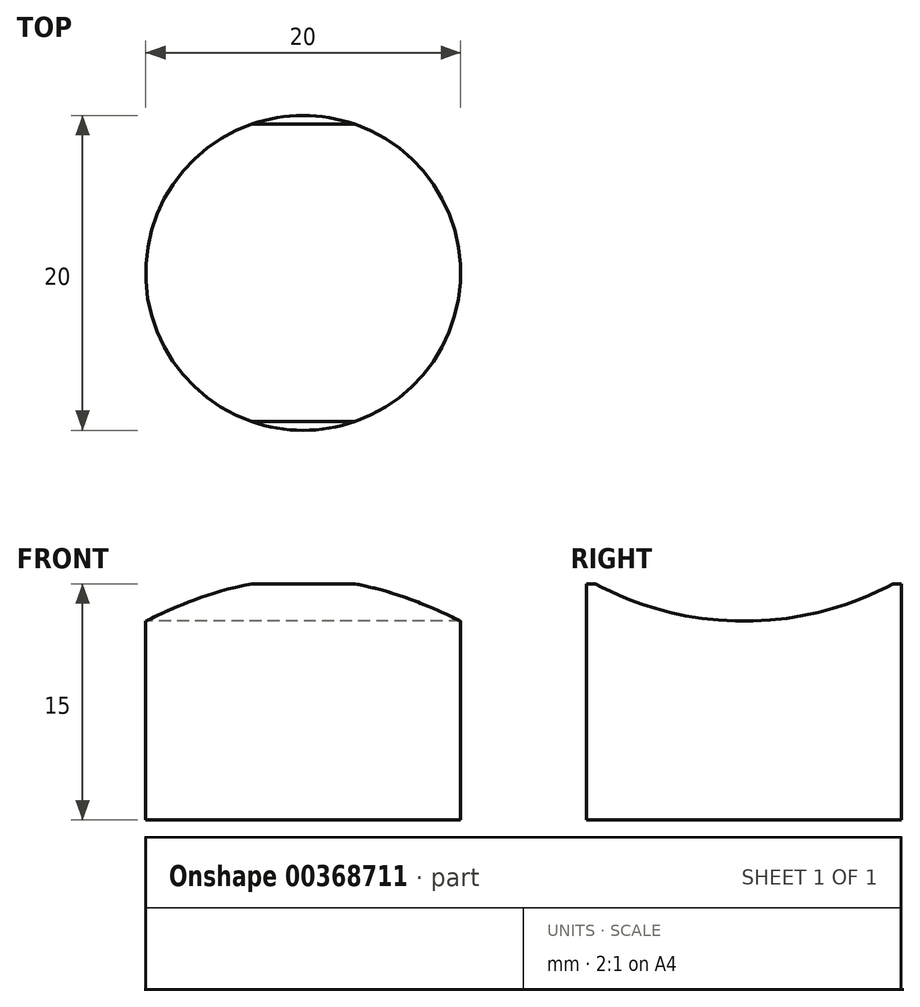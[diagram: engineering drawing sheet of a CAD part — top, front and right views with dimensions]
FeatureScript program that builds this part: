
annotation { "Feature Type Name" : "Feature", "Feature Type Description" : "" }
export const myFeature = defineFeature(function(context is Context, id is Id, definition is map)
    precondition{}
    {
        {
            var Q0;
            Q0=qCreatedBy(makeId("Top.planeOp"),FACE);
            var sketch = newSketch(context, id + "F0", { "sketchPlane" : qUnion([Q0])});
            skCircle(sketch, "E0", {"center": v(0, 0) * mm, "radius": 10 * mm});
            skSolve(sketch);
        }
        {
            var Q0;
            Q0 = qSketchRegion(id + "F0", true);
            extrude(context, id + "F1", {"entities" : qUnion([Q0]), "depth" : 15 * mm});
        }
        {
            var Q0;
            Q0=qCreatedBy(makeId("Right.planeOp"),FACE);
            var sketch = newSketch(context, id + "F2", { "sketchPlane" : qUnion([Q0])});
            skCircle(sketch, "E1", {"center": v(0, 32.63) * mm, "radius": 20 * mm});
            skSolve(sketch);
        }
        {
            var Q0;
            Q0 = qSketchRegion(id + "F2", true);
            extrude(context, id + "F3", {"entities" : qUnion([Q0]), "operationType" : NewBodyOperationType.REMOVE, "endBound" : BoundingType.SYMMETRIC, "depth" : 60.6 * mm});
        }
    });
